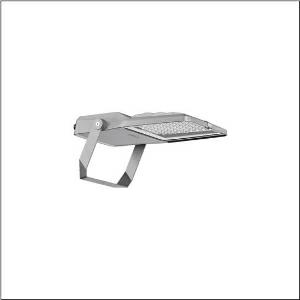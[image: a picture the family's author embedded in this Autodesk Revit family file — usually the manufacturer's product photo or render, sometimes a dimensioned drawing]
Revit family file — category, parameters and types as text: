
# Revit family: floodlight_fl_21_mini___pl33t_5xa7775d2f1a_0460
name_source: partatom
category: Lighting Fixtures
units: mm (PartAtom-declared; Revit-internal decimal feet)

## family parameters
Cut with Voids When Loaded = No
Host = Face
Light Source = No
Part Type = Normal
Room Calculation Point = No
Round Connector Dimension = Use Diameter
Shared = No

## types (1)
- --- (1 x LED, 17630 lm, 142.9 W, 3000K)
    Apparent Load = 143 VA
    CIE Flux Codes = 26 75 99 100 100
    Color Rendering = 70
    Color Temperature = 3000K
    Default Elevation = 1800 mm
    Description = Floodlight FL 21 mini, floodlight, primary light control with lens, of PMMA, primary optical cover: protective disc, of toughened safety glass, transparent, light distribution: PL33T, light emission: direct distribution, installation type: surface-mounted, LED, High Power LED, rated luminous flux: 17.630lm, luminous efficacy: 123lm/W, light colour: 730, colour temperature: 3000K, control gear: Smart Interface (Zhaga), control: flexible luminous flux parameterisation, time-dependent luminous flux control, constant luminous flux control, overheat protection, pre-setting: logarithmic dimming characteristic, with terminal, 6-pole, mains connection: 220..240V, AC, 50/60Hz, start of lifetime: 143W, end of service life: 151W, reduction: 63W, luminaire housing, of diecast aluminium, powder-coated, Siteco® metallic grey (DB 702S), corrosivity category C5 mid according to DIN EN ISO 12944, suitable for swimming pools, chlorine-resistant, sealing non-destructively replaceable, mounting bracket, of steel, galvanised, powder-coated, Siteco® metallic grey (DB 702S), Smart Interface above, protection rating (complete): IP66, insulation class (complete): insulation class II (safety insulation), certification: CE, ENEC, VDE, protection symbol: D, impact resistance: IK08, permissible operating ambient temperature: -40..+40°C, permissible operating ambient temperature for outdoor applications: -40..+50°C, standard: DIN EN 12944, LABS conformity tested according to VDMA 24364:2018-05, packaging unit: 1 piece

Light Distribution: PL33T
    Height = 70 mm
    Lamp = 1 x LED
    Lamp Light Flux = 17630 lm
    Lamp Power = 142.9 W
    Lamp count = 1
    Length = 485 mm
    Luminous efficacy = 123 lm/W
    Manufacturer = Siteco
    ModVariant = No
    Model = 5XA7775D2F1A
    Number of Poles = 1
    OnlyDefault = Yes
    Power Factor = 1
    Product Name = Floodlight FL 21 mini | PL33T
    Product group = floodlight | pylon annexe
    ProductGroupID = 6200
    Protection Class = Protection class II
    Protection Degree = IP 66
    RLX_Detail_Level = 1
    RLX_Emergency_Light_Flux = 0 lm
    RLX_Emergency_Type = 0
    RLX_Emergency_Type_DB = No
    RlxData = <blob elided: 96221 chars, md5=c5a8207a>
    Socket = socket
    Standby Power = 0 W
    System Light Flux = 17630 lm
    System Power = 143 W
    Type Comments = factory setting: luminous flux: 100 % | dim-lin: 254 | 730 mA
    Type Image = l_1006845.jpg
    URL = http://relux.com
    VarID = @adj_148442
    Voltage = 0 V
    Weight = 0.00 kg
    Width = 337 mm

## geometry (parser evidence)
native form markers: Blend x4, Sweep x12
no freeform markers — native parametric forms only
